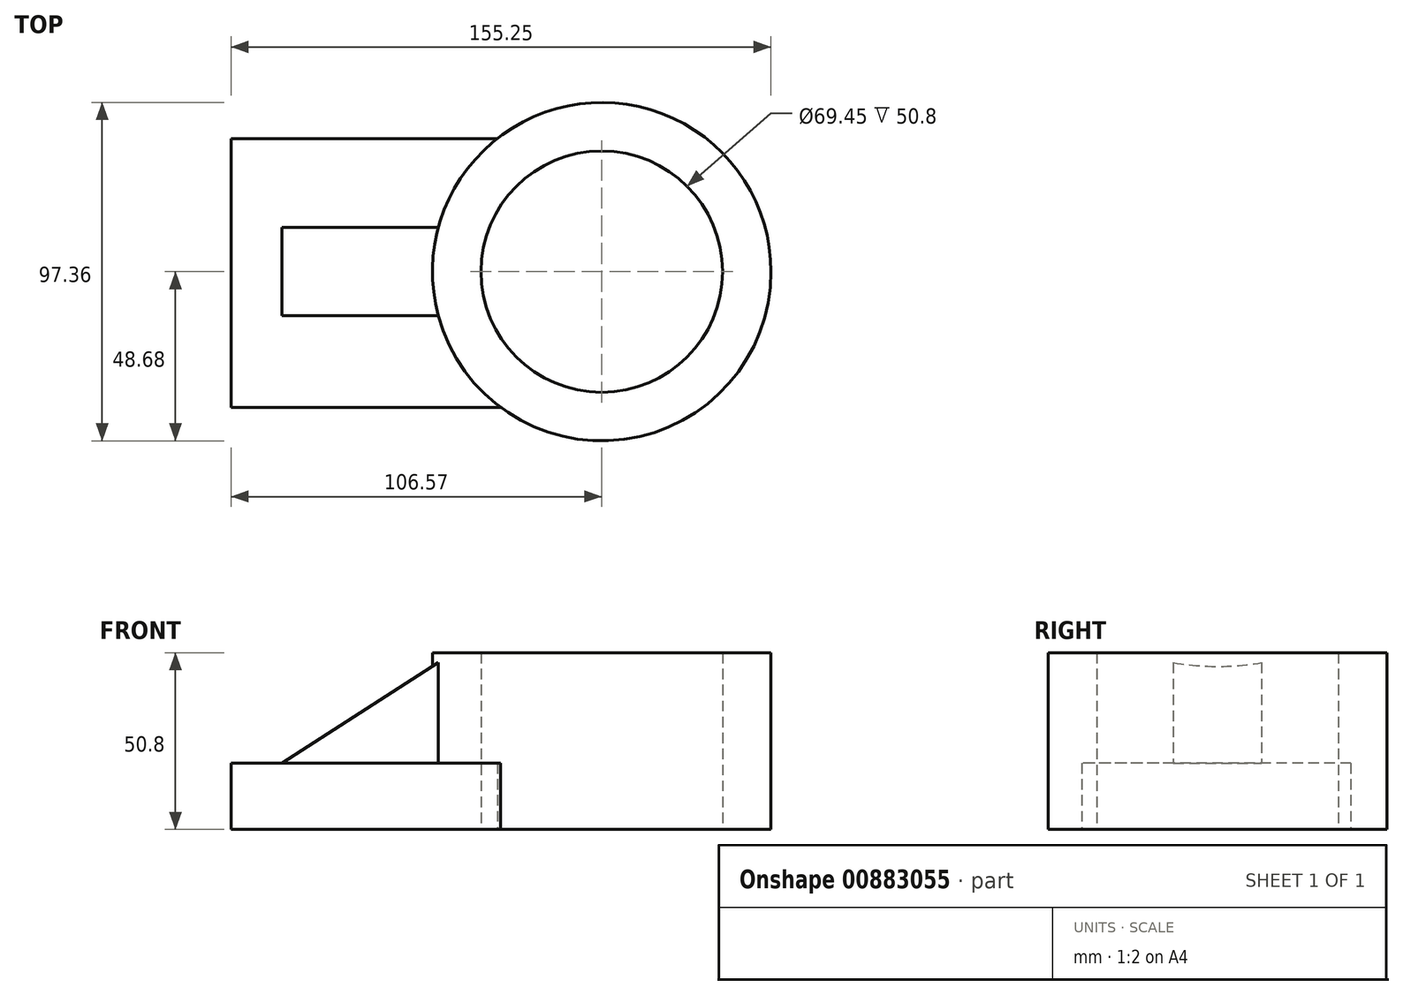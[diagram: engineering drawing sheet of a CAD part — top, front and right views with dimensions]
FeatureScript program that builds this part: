
annotation { "Feature Type Name" : "Feature", "Feature Type Description" : "" }
export const myFeature = defineFeature(function(context is Context, id is Id, definition is map)
    precondition{}
    {
        {
            var Q0;
            Q0=qCreatedBy(makeId("Top.planeOp"),FACE);
            var sketch = newSketch(context, id + "F0", { "sketchPlane" : qUnion([Q0])});
            skCircle(sketch, "E0", {"center": v(0, 0) * mm, "radius": 48.68 * mm});
            skCircle(sketch, "E1", {"center": v(0, 0) * mm, "radius": 34.73 * mm});
            skSolve(sketch);
        }
        {
            var Q0;
            Q0=makeQuery(id+"F0.imprint","IMPRINT",FACE,{"disambiguationData":[TD([[makeQuery(id+"F0.imprint","IMPRINT",EDGE,{"derivedFrom":sQuery(id+"F0.wireOp",EDGE,"E0")}),1.0]])]});
            extrude(context, id + "F1", {"entities" : qUnion([Q0]), "depth" : 50.8 * mm, "offsetDistance" : 25.4 * mm});
        }
        {
            var Q0;
            Q0=qCreatedBy(makeId("Top.planeOp"),FACE);
            var sketch = newSketch(context, id + "F2", { "sketchPlane" : qUnion([Q0])});
            skArc(sketch, "E2", {"start": v(-14.48, 38.32) * mm, "mid": v(-40.95, -1.07) * mm, "end": v(-12.46, -39.02) * mm});
            skLineSegment(sketch, "E3", {"start": v(-14.48, 38.32) * mm, "end": v(-106.57, 38.32) * mm});
            skLineSegment(sketch, "E4", {"start": v(-106.57, 38.32) * mm, "end": v(-106.57, -39.02) * mm});
            skLineSegment(sketch, "E5", {"start": v(-106.57, -39.02) * mm, "end": v(-12.46, -39.02) * mm});
            skSolve(sketch);
        }
        {
            var Q0;
            Q0=makeQuery(id+"F2.imprint","IMPRINT",FACE,{"disambiguationData":[TD([[makeQuery(id+"F2.imprint","IMPRINT",EDGE,{"derivedFrom":sQuery(id+"F2.wireOp",EDGE,"E2")}),-1.0]])]});
            extrude(context, id + "F3", {"entities" : qUnion([Q0]), "operationType" : NewBodyOperationType.ADD, "depth" : 19.05 * mm, "offsetDistance" : 25.4 * mm});
        }
        {
            var Q0;
            Q0=qCreatedBy(makeId("Front.planeOp"),FACE);
            var sketch = newSketch(context, id + "F4", { "sketchPlane" : qUnion([Q0])});
            skLineSegment(sketch, "E6", {"start": v(-46.43, 48.33) * mm, "end": v(-95.2, 16.98) * mm});
            skLineSegment(sketch, "E7", {"start": v(-95.2, 16.98) * mm, "end": v(-46.43, 16.98) * mm});
            skLineSegment(sketch, "E8", {"start": v(-46.43, 16.98) * mm, "end": v(-46.43, 48.33) * mm});
            skSolve(sketch);
        }
        {
            var Q0;
            Q0=makeQuery(id+"F4.imprint","IMPRINT",FACE,{"disambiguationData":[TD([[makeQuery(id+"F4.imprint","IMPRINT",EDGE,{"derivedFrom":sQuery(id+"F4.wireOp",EDGE,"E6")}),1.0]])]});
            extrude(context, id + "F5", {"entities" : qUnion([Q0]), "operationType" : NewBodyOperationType.ADD, "depth" : 12.7 * mm, "offsetDistance" : 25.4 * mm, "hasSecondDirection" : true, "secondDirectionOppositeDirection" : true, "secondDirectionDepth" : 12.7 * mm});
        }
    });
